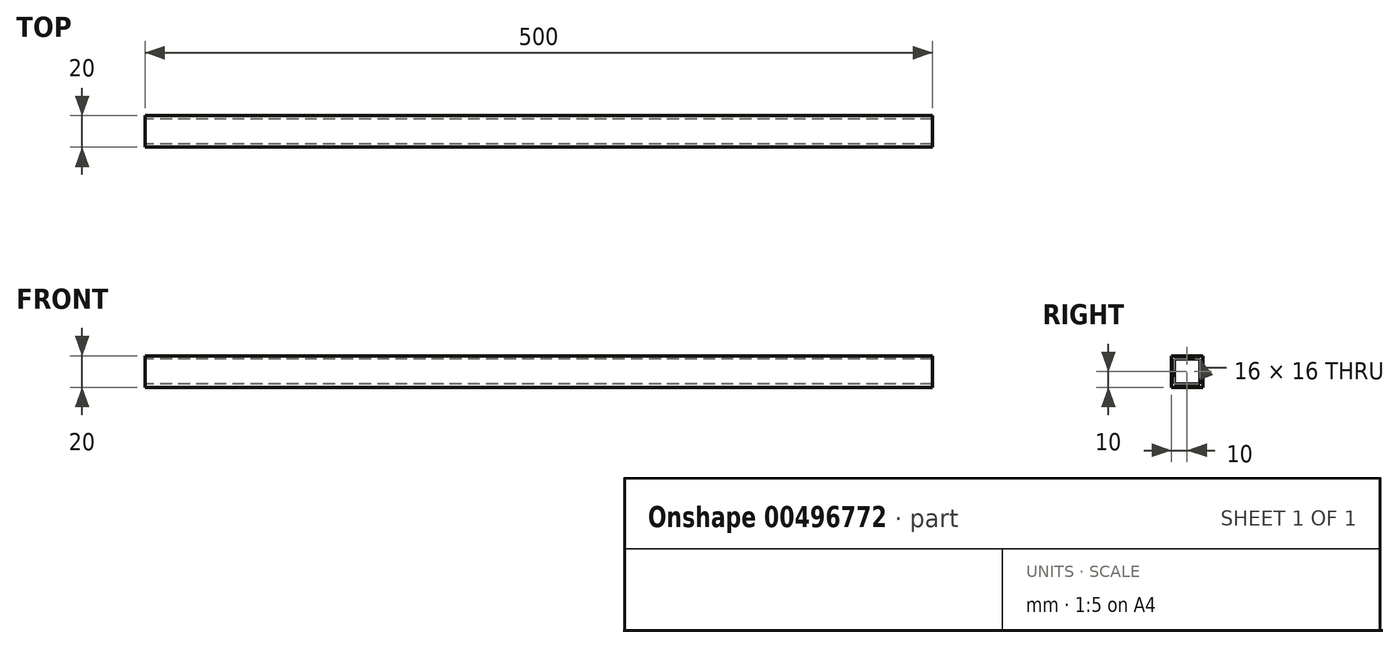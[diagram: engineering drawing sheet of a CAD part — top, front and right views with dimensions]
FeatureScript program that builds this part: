
annotation { "Feature Type Name" : "Feature", "Feature Type Description" : "" }
export const myFeature = defineFeature(function(context is Context, id is Id, definition is map)
    precondition{}
    {
        {
            var Q0;
            Q0=qCreatedBy(makeId("Right.planeOp"),FACE);
            var sketch = newSketch(context, id + "F0", { "sketchPlane" : qUnion([Q0])});
            skLineSegment(sketch, "E0.bottom", {"start": v(8, -8) * mm, "end": v(-8, -8) * mm});
            skLineSegment(sketch, "E0.top", {"start": v(8, 8) * mm, "end": v(-8, 8) * mm});
            skLineSegment(sketch, "E0.left", {"start": v(8, -8) * mm, "end": v(8, 8) * mm});
            skLineSegment(sketch, "E0.right", {"start": v(-8, -8) * mm, "end": v(-8, 8) * mm});
            skPoint(sketch, "E0.middle", {"position": v(0, 0) * mm});
            skLineSegment(sketch, "E1.bottom", {"start": v(10, -10) * mm, "end": v(-10, -10) * mm});
            skLineSegment(sketch, "E1.top", {"start": v(10, 10) * mm, "end": v(-10, 10) * mm});
            skLineSegment(sketch, "E1.left", {"start": v(10, -10) * mm, "end": v(10, 10) * mm});
            skLineSegment(sketch, "E1.right", {"start": v(-10, -10) * mm, "end": v(-10, 10) * mm});
            skSolve(sketch);
        }
        {
            var Q0;
            Q0=makeQuery(id+"F0.imprint","IMPRINT",FACE,{"disambiguationData":[TD([[makeQuery(id+"F0.imprint","IMPRINT",EDGE,{"derivedFrom":sQuery(id+"F0.wireOp",EDGE,"E0.bottom")}),1.0]])]});
            extrude(context, id + "F1", {"entities" : qUnion([Q0]), "depth" : 500 * mm, "offsetDistance" : 25 * mm});
        }
    });
